# Revit family: 06-44-0035-DN40-600
name_source: partatom
category: Pipe Accessories
units: mm (PartAtom-declared; Revit-internal decimal feet)

## family parameters
Always vertical = No
Cut with Voids When Loaded = No
OmniClass Number = 23.60.00.00
OmniClass Title = General Purpose: Services
Part Type = Valve - Breaks Into
Round Connector Dimension = Use Diameter
Shared = Yes
Work Plane-Based = No

## types (15) — shared parameters
Body_Wallthickness = 15 mm  [stored 0.0492126 ft]
DN040_PN10/16 = 06-040-44-0144299
DN050_PN10/16 = 06-050-44-0144299
DN065_PN10/16 = 06-065-44-0144299
DN080_PN10/16 = 06-080-44-0144299
DN100_PN10/16 = 06-100-44-0144299
DN125_PN10/16 = 06-125-44-0144299
DN150_PN10/16 = 06-150-44-0144299
DN200_PN10 = 06-200-44-0044299
DN200_PN16 = 06-200-44-0144299
DN250_PN10 = 06-250-44-0044299
DN250_PN16 = 06-250-44-0144299
DN300_PN10 = 06-300-44-0044287
DN300_PN16 = 06-300-44-0144287
DN350_PN10 = 06-350-44-00442
DN350_PN16 = 06-350-44-01442
DN400_PN10 = 06-400-44-00442
DN400_PN16 = 06-400-44-01442
DN450_PN10 = 06-450-44-00442
DN450_PN16 = 06-450-44-01442
DN500_PN10 = 06-500-44-00442
DN500_PN16 = 06-500-44-01442
DN600_PN10 = 06-600-44-00442
DN600_PN16 = 06-600-44-01442
Ftc = 4 mm  [stored 0.0131234 ft]
Gearbox_Flangethickness = 10 mm  [stored 0.0328084 ft]
Name_Height_reference = 10 mm  [stored 0.0328084 ft]
Rib_Thickness = 18 mm  [stored 0.0590551 ft]
Search_table = 06-44-0035-DN40-600
Tf = 26 mm
URL product pages = https://www.avkvalves.com
zero-valued in all types: Bottom_Reference

## per-type parameters (varying)
- DN 040: At=57 mm; Body_Height=100 mm; Body_depth=113 mm; Body_width=58 mm; Bonnet_Flange_Depth=127 mm; Bonnet_Flange_Width=90 mm; Bonnet_Flange_cut=8 mm  [stored 0.0262467 ft]; Bonnet_Flange_thickness=15 mm  [stored 0.0492126 ft]; Bonnet_Height=38 mm; Bonnet_Reference_height=90 mm; Bonnet_Thickness=59 mm; Bt=59 mm; Bt_2=52 mm; CL=54 mm; CL _Thickness=10 mm  [stored 0.0328084 ft]; CL_2=24 mm  [stored 0.0787402 ft]; CL_Thickness 2=5 mm  [stored 0.0164042 ft]; Cut_Reference=280 mm; DN 040=Yes; DN 050=No; DN 065=No; DN 080=No; DN 100=No; DN 125=No; DN 150=No; DN 200=No; DN 250=No; DN 300=No; DN 350=No; DN 400=No; DN 450=No; DN 500=No; DN 600=No; Description_=AVK_GATE_VALVE,FLANGED; F=7 mm  [stored 0.0229659 ft]; F1=8 mm  [stored 0.0262467 ft]; F2=30 mm  [stored 0.0984252 ft]; Fillet_Thickness=6 mm  [stored 0.019685 ft]; Flange_OR=75 mm; Flange_Thickness=19 mm  [stored 0.062336 ft]; Flange_Thickness_cut=28 mm  [stored 0.0918635 ft]; Ftc_reference_height=75 mm; Gearbox_Flange_Dia=10 mm  [stored 0.0328084 ft]; H=194 mm; H3=269 mm; Horizontal_Flange_width=150 mm; ID (Radius)=20 mm  [stored 0.0656168 ft]; L=140 mm; L_Dia=40 mm  [stored 0.131234 ft]; Name_Reference=80 mm; Name_Width=29 mm  [stored 0.0951444 ft]; Nominal Diameter (DN)=40 mm  [stored 0.131234 ft]; R1tv=750 mm; R2f=15 mm  [stored 0.0492126 ft]; RF_Dia=42 mm  [stored 0.137795 ft]; Rf=250 mm; Rib_Height_Reference_1=120 mm; Rib_Height_Reference_2=110 mm; Rib_Height_Reference_3=100 mm; Rib_Height_Reference_4=40 mm  [stored 0.131234 ft]; Rib_Width_1=29 mm  [stored 0.0951444 ft]; Rib_Width_2=29 mm  [stored 0.0951444 ft]; Rib_Width_3=29 mm  [stored 0.0951444 ft]; Rib_depth_1=29 mm  [stored 0.0951444 ft]; Rib_depth_2=29 mm  [stored 0.0951444 ft]; Rib_depth_3=29 mm  [stored 0.0951444 ft]; Rt=250 mm
- DN 050: At=61 mm; Body_Height=110 mm; Body_depth=121 mm; Body_width=58 mm; Bonnet_Flange_Depth=133 mm; Bonnet_Flange_Width=92 mm; Bonnet_Flange_cut=8 mm  [stored 0.0262467 ft]; Bonnet_Flange_thickness=15 mm  [stored 0.0492126 ft]; Bonnet_Height=41 mm; Bonnet_Reference_height=100 mm; Bonnet_Thickness=59 mm; Bt=59 mm; Bt_2=52 mm; CL=58 mm; CL _Thickness=10 mm  [stored 0.0328084 ft]; CL_2=28 mm  [stored 0.0918635 ft]; CL_Thickness 2=6 mm  [stored 0.019685 ft]; Cut_Reference=300 mm; DN 040=No; DN 050=Yes; DN 065=No; DN 080=No; DN 100=No; DN 125=No; DN 150=No; DN 200=No; DN 250=No; DN 300=No; DN 350=No; DN 400=No; DN 450=No; DN 500=No; DN 600=No; Description_=AVK_GATE_VALVE,FLANGED; F=7 mm  [stored 0.0229659 ft]; F1=8 mm  [stored 0.0262467 ft]; F2=30 mm  [stored 0.0984252 ft]; Fillet_Thickness=6 mm  [stored 0.019685 ft]; Flange_OR=83 mm; Flange_Thickness=19 mm  [stored 0.062336 ft]; Flange_Thickness_cut=29 mm  [stored 0.0951444 ft]; Ftc_reference_height=83 mm; Gearbox_Flange_Dia=10 mm  [stored 0.0328084 ft]; H=208 mm; H3=290 mm; Horizontal_Flange_width=164 mm; ID (Radius)=25 mm  [stored 0.082021 ft]; L=150 mm; L_Dia=50 mm; Name_Reference=90 mm; Name_Width=29 mm  [stored 0.0951444 ft]; Nominal Diameter (DN)=50 mm; R1tv=825 mm; R2f=15 mm  [stored 0.0492126 ft]; RF_Dia=50 mm; Rf=273 mm; Rib_Height_Reference_1=120 mm; Rib_Height_Reference_2=110 mm; Rib_Height_Reference_3=100 mm; Rib_Height_Reference_4=60 mm; Rib_Width_1=29 mm  [stored 0.0951444 ft]; Rib_Width_2=29 mm  [stored 0.0951444 ft]; Rib_Width_3=29 mm  [stored 0.0951444 ft]; Rib_depth_1=29 mm  [stored 0.0951444 ft]; Rib_depth_2=29 mm  [stored 0.0951444 ft]; Rib_depth_3=29 mm  [stored 0.0951444 ft]; Rt=275 mm
- DN 065: At=69 mm; Body_Height=125 mm; Body_depth=137 mm; Body_width=59 mm; Bonnet_Flange_Depth=152 mm; Bonnet_Flange_Width=91 mm; Bonnet_Flange_cut=8 mm  [stored 0.0262467 ft]; Bonnet_Flange_thickness=15 mm  [stored 0.0492126 ft]; Bonnet_Height=46 mm; Bonnet_Reference_height=115 mm; Bonnet_Thickness=60 mm; Bt=60 mm; Bt_2=53 mm; CL=75 mm; CL _Thickness=10 mm  [stored 0.0328084 ft]; CL_2=45 mm  [stored 0.147638 ft]; CL_Thickness 2=5 mm  [stored 0.0164042 ft]; Cut_Reference=340 mm; DN 040=No; DN 050=No; DN 065=Yes; DN 080=Yes; DN 100=Yes; DN 125=Yes; DN 150=Yes; DN 200=Yes; DN 250=Yes; DN 300=Yes; DN 350=Yes; DN 400=Yes; DN 450=Yes; DN 500=Yes; DN 600=Yes; Description_=AVK_GATE-VALVE,FLANGED; F=9 mm; F1=10 mm  [stored 0.0328084 ft]; F2=34 mm  [stored 0.111549 ft]; Fillet_Thickness=6 mm  [stored 0.019685 ft]; Flange_OR=93 mm; Flange_Thickness=19 mm  [stored 0.062336 ft]; Flange_Thickness_cut=30 mm  [stored 0.0984252 ft]; Ftc_reference_height=93 mm; Gearbox_Flange_Dia=10 mm  [stored 0.0328084 ft]; H=244 mm; H3=337 mm; Horizontal_Flange_width=186 mm; ID (Radius)=33 mm; L=170 mm; L_Dia=65 mm; Name_Reference=100 mm; Name_Width=30 mm  [stored 0.0984252 ft]; Nominal Diameter (DN)=65 mm; R1tv=925 mm; R2f=15 mm  [stored 0.0492126 ft]; RF_Dia=59 mm; Rf=310 mm; Rib_Height_Reference_1=120 mm; Rib_Height_Reference_2=110 mm; Rib_Height_Reference_3=100 mm; Rib_Height_Reference_4=75 mm; Rib_Width_1=30 mm  [stored 0.0984252 ft]; Rib_Width_2=30 mm  [stored 0.0984252 ft]; Rib_Width_3=30 mm  [stored 0.0984252 ft]; Rib_depth_1=30 mm  [stored 0.0984252 ft]; Rib_depth_2=30 mm  [stored 0.0984252 ft]; Rib_depth_3=30 mm  [stored 0.0984252 ft]; Rt=308 mm
- DN 080: At=70 mm; Body_Height=155 mm; Body_depth=140 mm; Body_width=58 mm; Bonnet_Flange_Depth=171 mm; Bonnet_Flange_Width=96 mm; Bonnet_Flange_cut=8 mm  [stored 0.0262467 ft]; Bonnet_Flange_thickness=15 mm  [stored 0.0492126 ft]; Bonnet_Height=50 mm; Bonnet_Reference_height=145 mm; Bonnet_Thickness=59 mm; Bt=59 mm; Bt_2=52 mm; CL=83 mm; CL _Thickness=11 mm  [stored 0.0360892 ft]; CL_2=53 mm; CL_Thickness 2=7 mm  [stored 0.0229659 ft]; Cut_Reference=360 mm; DN 040=Yes; DN 050=Yes; DN 065=Yes; DN 080=Yes; DN 100=Yes; DN 125=Yes; DN 150=Yes; DN 200=Yes; DN 250=Yes; DN 300=Yes; DN 350=Yes; DN 400=Yes; DN 450=Yes; DN 500=Yes; DN 600=Yes; Description_=AVK_GATE_VALVE,FLANGED; F=9 mm; F1=10 mm  [stored 0.0328084 ft]; F2=34 mm  [stored 0.111549 ft]; Fillet_Thickness=6 mm  [stored 0.019685 ft]; Flange_OR=100 mm; Flange_Thickness=19 mm  [stored 0.062336 ft]; Flange_Thickness_cut=30 mm  [stored 0.0984252 ft]; Ftc_reference_height=100 mm; Gearbox_Flange_Dia=11 mm  [stored 0.0360892 ft]; H=282 mm; H3=382 mm; Horizontal_Flange_width=200 mm; ID (Radius)=40 mm  [stored 0.131234 ft]; L=180 mm; L_Dia=80 mm; Name_Reference=130 mm; Name_Width=29 mm  [stored 0.0951444 ft]; Nominal Diameter (DN)=80 mm; R1tv=1000 mm; R2f=15 mm  [stored 0.0492126 ft]; RF_Dia=66 mm; Rf=333 mm; Rib_Height_Reference_1=120 mm; Rib_Height_Reference_2=110 mm; Rib_Height_Reference_3=100 mm; Rib_Height_Reference_4=85 mm; Rib_Width_1=29 mm  [stored 0.0951444 ft]; Rib_Width_2=29 mm  [stored 0.0951444 ft]; Rib_Width_3=29 mm  [stored 0.0951444 ft]; Rib_depth_1=29 mm  [stored 0.0951444 ft]; Rib_depth_2=29 mm  [stored 0.0951444 ft]; Rib_depth_3=29 mm  [stored 0.0951444 ft]; Rt=333 mm
- DN 100: At=84 mm; Body_Height=175 mm; Body_depth=168 mm; Body_width=58 mm; Bonnet_Flange_Depth=192 mm; Bonnet_Flange_Width=105 mm; Bonnet_Flange_cut=8 mm  [stored 0.0262467 ft]; Bonnet_Flange_thickness=15 mm  [stored 0.0492126 ft]; Bonnet_Height=55 mm; Bonnet_Reference_height=165 mm; Bonnet_Thickness=59 mm; Bt=59 mm; Bt_2=52 mm; CL=86 mm; CL _Thickness=12 mm  [stored 0.0393701 ft]; CL_2=56 mm; CL_Thickness 2=10 mm  [stored 0.0328084 ft]; Cut_Reference=380 mm; DN 040=Yes; DN 050=Yes; DN 065=Yes; DN 080=Yes; DN 100=Yes; DN 125=Yes; DN 150=Yes; DN 200=Yes; DN 250=Yes; DN 300=Yes; DN 350=Yes; DN 400=Yes; DN 450=Yes; DN 500=Yes; DN 600=Yes; Description_=AVK_GATE_VALVE,FLANGED; F=10 mm  [stored 0.0328084 ft]; F1=11 mm  [stored 0.0360892 ft]; F2=34 mm  [stored 0.111549 ft]; Fillet_Thickness=6 mm  [stored 0.019685 ft]; Flange_OR=110 mm; Flange_Thickness=19 mm  [stored 0.062336 ft]; Flange_Thickness_cut=30 mm  [stored 0.0984252 ft]; Ftc_reference_height=110 mm; Gearbox_Flange_Dia=12 mm  [stored 0.0393701 ft]; H=305 mm; H3=415 mm; Horizontal_Flange_width=220 mm; ID (Radius)=50 mm; L=190 mm; L_Dia=100 mm; Name_Reference=150 mm; Name_Width=29 mm  [stored 0.0951444 ft]; Nominal Diameter (DN)=100 mm; R1tv=1095 mm; R2f=15 mm  [stored 0.0492126 ft]; RF_Dia=78 mm; Rf=367 mm; Rib_Height_Reference_1=120 mm; Rib_Height_Reference_2=110 mm; Rib_Height_Reference_3=100 mm; Rib_Height_Reference_4=90 mm; Rib_Width_1=29 mm  [stored 0.0951444 ft]; Rib_Width_2=29 mm  [stored 0.0951444 ft]; Rib_Width_3=29 mm  [stored 0.0951444 ft]; Rib_depth_1=29 mm  [stored 0.0951444 ft]; Rib_depth_2=29 mm  [stored 0.0951444 ft]; Rib_depth_3=29 mm  [stored 0.0951444 ft]; Rt=365 mm
- DN 150: At=121 mm; Body_Height=200 mm; Body_depth=242 mm; Body_width=70 mm; Bonnet_Flange_Depth=272 mm; Bonnet_Flange_Width=130 mm; Bonnet_Flange_cut=8 mm  [stored 0.0262467 ft]; Bonnet_Flange_thickness=15 mm  [stored 0.0492126 ft]; Bonnet_Height=71 mm; Bonnet_Reference_height=190 mm; Bonnet_Thickness=71 mm; Bt=71 mm; Bt_2=64 mm; CL=156 mm; CL _Thickness=16 mm  [stored 0.0524934 ft]; CL_2=126 mm; CL_Thickness 2=18 mm  [stored 0.0590551 ft]; Cut_Reference=420 mm; DN 040=Yes; DN 050=Yes; DN 065=Yes; DN 080=Yes; DN 100=Yes; DN 125=Yes; DN 150=Yes; DN 200=Yes; DN 250=Yes; DN 300=Yes; DN 350=Yes; DN 400=Yes; DN 450=Yes; DN 500=Yes; DN 600=Yes; Description_=AVK_GATE_VALVE,FLANGED; F=10 mm  [stored 0.0328084 ft]; F1=11 mm  [stored 0.0360892 ft]; F2=34 mm  [stored 0.111549 ft]; Fillet_Thickness=12 mm  [stored 0.0393701 ft]; Flange_OR=143 mm; Flange_Thickness=19 mm  [stored 0.062336 ft]; Flange_Thickness_cut=34 mm  [stored 0.111549 ft]; Ftc_reference_height=143 mm; Gearbox_Flange_Dia=16 mm  [stored 0.0524934 ft]; H=400 mm; H3=543 mm; Horizontal_Flange_width=286 mm; ID (Radius)=75 mm; L=210 mm; L_Dia=150 mm; Name_Reference=170 mm; Name_Width=35 mm  [stored 0.114829 ft]; Nominal Diameter (DN)=150 mm; R1tv=1425 mm; R2f=30 mm  [stored 0.0984252 ft]; RF_Dia=106 mm; Rf=477 mm; Rib_Height_Reference_1=120 mm; Rib_Height_Reference_2=110 mm; Rib_Height_Reference_3=100 mm; Rib_Height_Reference_4=150 mm; Rib_Width_1=35 mm  [stored 0.114829 ft]; Rib_Width_2=35 mm  [stored 0.114829 ft]; Rib_Width_3=35 mm  [stored 0.114829 ft]; Rib_depth_1=35 mm  [stored 0.114829 ft]; Rib_depth_2=35 mm  [stored 0.114829 ft]; Rib_depth_3=35 mm  [stored 0.114829 ft]; Rt=475 mm
- DN 200: At=157 mm; Body_Height=250 mm; Body_depth=314 mm; Body_width=110 mm; Bonnet_Flange_Depth=332 mm; Bonnet_Flange_Width=170 mm; Bonnet_Flange_cut=13 mm; Bonnet_Flange_thickness=25 mm  [stored 0.082021 ft]; Bonnet_Height=85 mm; Bonnet_Reference_height=240 mm; Bonnet_Thickness=112 mm; Bt=112 mm; Bt_2=104 mm; CL=196 mm; CL _Thickness=23 mm; CL_2=166 mm; CL_Thickness 2=32 mm  [stored 0.104987 ft]; Cut_Reference=460 mm; DN 040=Yes; DN 050=Yes; DN 065=Yes; DN 080=Yes; DN 100=Yes; DN 125=Yes; DN 150=Yes; DN 200=Yes; DN 250=Yes; DN 300=Yes; DN 350=Yes; DN 400=Yes; DN 450=Yes; DN 500=Yes; DN 600=Yes; Description_=AVK_GATE_VALVE,FLANGED; F=12 mm  [stored 0.0393701 ft]; F1=14 mm  [stored 0.0459318 ft]; F2=34 mm  [stored 0.111549 ft]; Fillet_Thickness=24 mm  [stored 0.0787402 ft]; Flange_OR=170 mm; Flange_Thickness=20 mm  [stored 0.0656168 ft]; Flange_Thickness_cut=35 mm  [stored 0.114829 ft]; Ftc_reference_height=170 mm; Gearbox_Flange_Dia=23 mm; H=490 mm; H3=660 mm; Horizontal_Flange_width=340 mm; ID (Radius)=100 mm; L=230 mm; L_Dia=200 mm; Name_Reference=200 mm; Name_Width=55 mm; Nominal Diameter (DN)=200 mm; R1tv=1700 mm; R2f=60 mm; RF_Dia=133 mm; Rf=567 mm; Rib_Height_Reference_1=120 mm; Rib_Height_Reference_2=110 mm; Rib_Height_Reference_3=100 mm; Rib_Height_Reference_4=180 mm; Rib_Width_1=55 mm; Rib_Width_2=55 mm; Rib_Width_3=55 mm; Rib_depth_1=55 mm; Rib_depth_2=55 mm; Rib_depth_3=55 mm; Rt=567 mm
- DN 250: At=196 mm; Body_Height=320 mm; Body_depth=392 mm; Body_width=132 mm; Bonnet_Flange_Depth=422 mm; Bonnet_Flange_Width=175 mm; Bonnet_Flange_cut=13 mm; Bonnet_Flange_thickness=25 mm  [stored 0.082021 ft]; Bonnet_Height=100 mm; Bonnet_Reference_height=310 mm; Bonnet_Thickness=135 mm; Bt=135 mm; Bt_2=126 mm; CL=248 mm; CL _Thickness=24 mm  [stored 0.0787402 ft]; CL_2=218 mm; CL_Thickness 2=33 mm; Cut_Reference=500 mm; DN 040=Yes; DN 050=Yes; DN 065=Yes; DN 080=Yes; DN 100=Yes; DN 125=Yes; DN 150=Yes; DN 200=Yes; DN 250=Yes; DN 300=Yes; DN 350=Yes; DN 400=Yes; DN 450=Yes; DN 500=Yes; DN 600=Yes; Description_=AVK_GATE_VALVE,FLANGED; F=14 mm  [stored 0.0459318 ft]; F1=14 mm  [stored 0.0459318 ft]; F2=47 mm; Fillet_Thickness=24 mm  [stored 0.0787402 ft]; Flange_OR=200 mm; Flange_Thickness=22 mm  [stored 0.0721785 ft]; Flange_Thickness_cut=38 mm; Ftc_reference_height=200 mm; Gearbox_Flange_Dia=24 mm  [stored 0.0787402 ft]; H=625 mm; H3=864 mm; Horizontal_Flange_width=478 mm; ID (Radius)=125 mm; L=250 mm; L_Dia=250 mm; Name_Reference=200 mm; Name_Width=66 mm; Nominal Diameter (DN)=250 mm; R1tv=2000 mm; R2f=60 mm; RF_Dia=160 mm; Rf=797 mm; Rib_Height_Reference_1=90 mm; Rib_Height_Reference_2=110 mm; Rib_Height_Reference_3=100 mm; Rib_Height_Reference_4=250 mm; Rib_Width_1=150 mm; Rib_Width_2=66 mm; Rib_Width_3=66 mm; Rib_depth_1=422 mm; Rib_depth_2=66 mm; Rib_depth_3=66 mm; Rt=667 mm
- DN 300: At=209 mm; Body_Height=415 mm; Body_depth=418 mm; Body_width=160 mm; Bonnet_Flange_Depth=448 mm; Bonnet_Flange_Width=200 mm; Bonnet_Flange_cut=18 mm  [stored 0.0590551 ft]; Bonnet_Flange_thickness=35 mm  [stored 0.114829 ft]; Bonnet_Height=114 mm; Bonnet_Reference_height=405 mm; Bonnet_Thickness=163 mm; Bt=163 mm; Bt_2=154 mm; CL=234 mm; CL _Thickness=28 mm  [stored 0.0918635 ft]; CL_2=204 mm; CL_Thickness 2=42 mm  [stored 0.137795 ft]; Cut_Reference=540 mm; DN 040=Yes; DN 050=Yes; DN 065=Yes; DN 080=Yes; DN 100=Yes; DN 125=Yes; DN 150=Yes; DN 200=Yes; DN 250=Yes; DN 300=Yes; DN 350=Yes; DN 400=Yes; DN 450=Yes; DN 500=Yes; DN 600=Yes; Description_=AVK_GATE_VALVE,FLANGED; F=14 mm  [stored 0.0459318 ft]; F1=14 mm  [stored 0.0459318 ft]; F2=47 mm; Fillet_Thickness=24 mm  [stored 0.0787402 ft]; Flange_OR=228 mm; Flange_Thickness=25 mm  [stored 0.082021 ft]; Flange_Thickness_cut=39 mm  [stored 0.127953 ft]; Ftc_reference_height=228 mm; Gearbox_Flange_Dia=28 mm  [stored 0.0918635 ft]; H=706 mm; H3=928 mm; Horizontal_Flange_width=444 mm; ID (Radius)=150 mm; L=270 mm; L_Dia=300 mm; Name_Reference=300 mm; Name_Width=80 mm; Nominal Diameter (DN)=300 mm; R1tv=2275 mm; R2f=60 mm; RF_Dia=185 mm; Rf=740 mm; Rib_Height_Reference_1=113 mm; Rib_Height_Reference_2=285 mm; Rib_Height_Reference_3=100 mm; Rib_Height_Reference_4=325 mm; Rib_Width_1=210 mm; Rib_Width_2=210 mm; Rib_Width_3=80 mm; Rib_depth_1=455 mm; Rib_depth_2=455 mm; Rib_depth_3=80 mm; Rt=758 mm
- DN 350: At=238 mm; Body_Height=550 mm; Body_depth=476 mm; Body_width=150 mm; Bonnet_Flange_Depth=550 mm; Bonnet_Flange_Width=170 mm; Bonnet_Flange_cut=18 mm  [stored 0.0590551 ft]; Bonnet_Flange_thickness=35 mm  [stored 0.114829 ft]; Bonnet_Height=130 mm; Bonnet_Reference_height=540 mm; Bonnet_Thickness=153 mm; Bt=153 mm; Bt_2=144 mm; CL=315 mm; CL _Thickness=23 mm; CL_2=285 mm; CL_Thickness 2=32 mm  [stored 0.104987 ft]; Cut_Reference=580 mm; DN 040=Yes; DN 050=Yes; DN 065=Yes; DN 080=Yes; DN 100=Yes; DN 125=Yes; DN 150=Yes; DN 200=Yes; DN 250=Yes; DN 300=Yes; DN 350=Yes; DN 400=Yes; DN 450=Yes; DN 500=Yes; DN 600=Yes; Description_=AVK_GATE_VALVE,FLANGED; F=16 mm  [stored 0.0524934 ft]; F1=19 mm  [stored 0.062336 ft]; F2=55 mm; Fillet_Thickness=24 mm  [stored 0.0787402 ft]; Flange_OR=260 mm; Flange_Thickness=27 mm  [stored 0.0885827 ft]; Flange_Thickness_cut=43 mm; Ftc_reference_height=260 mm; Gearbox_Flange_Dia=23 mm; H=930 mm; H3=1190 mm; Horizontal_Flange_width=520 mm; ID (Radius)=175 mm; L=290 mm; L_Dia=350 mm; Name_Reference=520 mm; Name_Width=75 mm; Nominal Diameter (DN)=350 mm; R1tv=2600 mm; R2f=60 mm; RF_Dia=215 mm; Rf=867 mm; Rib_Height_Reference_1=84 mm; Rib_Height_Reference_2=204 mm; Rib_Height_Reference_3=338 mm; Rib_Height_Reference_4=459 mm; Rib_Width_1=180 mm; Rib_Width_2=180 mm; Rib_Width_3=180 mm; Rib_depth_1=564 mm; Rib_depth_2=564 mm; Rib_depth_3=564 mm; Rt=867 mm
- DN 400: At=238 mm; Body_Height=535 mm; Body_depth=476 mm; Body_width=150 mm; Bonnet_Flange_Depth=550 mm; Bonnet_Flange_Width=170 mm; Bonnet_Flange_cut=35 mm  [stored 0.114829 ft]; Bonnet_Flange_thickness=70 mm; Bonnet_Height=145 mm; Bonnet_Reference_height=525 mm; Bonnet_Thickness=153 mm; Bt=153 mm; Bt_2=144 mm; CL=360 mm; CL _Thickness=23 mm; CL_2=330 mm; CL_Thickness 2=32 mm  [stored 0.104987 ft]; Cut_Reference=620 mm; DN 040=Yes; DN 050=Yes; DN 065=Yes; DN 080=Yes; DN 100=Yes; DN 125=Yes; DN 150=Yes; DN 200=Yes; DN 250=Yes; DN 300=Yes; DN 350=Yes; DN 400=Yes; DN 450=Yes; DN 500=Yes; DN 600=Yes; Description_=AVK_GATE_VALVE,FLANGED; F=16 mm  [stored 0.0524934 ft]; F1=19 mm  [stored 0.062336 ft]; F2=55 mm; Fillet_Thickness=32 mm  [stored 0.104987 ft]; Flange_OR=290 mm; Flange_Thickness=28 mm  [stored 0.0918635 ft]; Flange_Thickness_cut=45 mm  [stored 0.147638 ft]; Ftc_reference_height=290 mm; Gearbox_Flange_Dia=23 mm; H=960 mm; H3=1241 mm; Horizontal_Flange_width=562 mm; ID (Radius)=200 mm; L=310 mm; L_Dia=400 mm; Name_Reference=475 mm; Name_Width=75 mm; Nominal Diameter (DN)=400 mm; R1tv=2900 mm; R2f=80 mm; RF_Dia=240 mm; Rf=937 mm; Rib_Height_Reference_1=91 mm; Rib_Height_Reference_2=230 mm; Rib_Height_Reference_3=380 mm; Rib_Height_Reference_4=492 mm; Rib_Width_1=180 mm; Rib_Width_2=180 mm; Rib_Width_3=180 mm; Rib_depth_1=564 mm; Rib_depth_2=564 mm; Rib_depth_3=564 mm; Rt=967 mm
- DN 450: At=381 mm; Body_Height=650 mm; Body_depth=762 mm; Body_width=140 mm; Bonnet_Flange_Depth=814 mm; Bonnet_Flange_Width=165 mm; Bonnet_Flange_cut=35 mm  [stored 0.114829 ft]; Bonnet_Flange_thickness=70 mm; Bonnet_Height=160 mm; Bonnet_Reference_height=640 mm; Bonnet_Thickness=143 mm; Bt=143 mm; Bt_2=134 mm; CL=427 mm; CL _Thickness=22 mm  [stored 0.0721785 ft]; CL_2=397 mm; CL_Thickness 2=30 mm  [stored 0.0984252 ft]; Cut_Reference=700 mm; DN 040=Yes; DN 050=Yes; DN 065=Yes; DN 080=Yes; DN 100=Yes; DN 125=Yes; DN 150=Yes; DN 200=Yes; DN 250=Yes; DN 300=Yes; DN 350=Yes; DN 400=Yes; DN 450=Yes; DN 500=Yes; DN 600=Yes; Description_=AVK_GATE_VALVE,FLANGED; F=15 mm  [stored 0.0492126 ft]; F1=19 mm  [stored 0.062336 ft]; F2=75 mm; Fillet_Thickness=32 mm  [stored 0.104987 ft]; Flange_OR=320 mm; Flange_Thickness=30 mm  [stored 0.0984252 ft]; Flange_Thickness_cut=48 mm; Ftc_reference_height=320 mm; Gearbox_Flange_Dia=88 mm; H=1162 mm; H3=1500 mm; Horizontal_Flange_width=676 mm; ID (Radius)=225 mm; L=350 mm; L_Dia=450 mm; Name_Reference=590 mm; Name_Width=70 mm; Nominal Diameter (DN)=450 mm; R1tv=3200 mm; R2f=80 mm; RF_Dia=274 mm; Rf=1127 mm; Rib_Height_Reference_1=172 mm; Rib_Height_Reference_2=310 mm; Rib_Height_Reference_3=475 mm; Rib_Height_Reference_4=595 mm; Rib_Width_1=165 mm; Rib_Width_2=165 mm; Rib_Width_3=165 mm; Rib_depth_1=814 mm; Rib_depth_2=814 mm; Rib_depth_3=814 mm; Rt=1067 mm
- DN 500: At=360 mm; Body_Height=650 mm; Body_depth=719 mm; Body_width=187 mm; Bonnet_Flange_Depth=792 mm; Bonnet_Flange_Width=219 mm; Bonnet_Flange_cut=35 mm  [stored 0.114829 ft]; Bonnet_Flange_thickness=70 mm; Bonnet_Height=179 mm; Bonnet_Reference_height=640 mm; Bonnet_Thickness=191 mm; Bt=191 mm; Bt_2=181 mm; CL=401 mm; CL _Thickness=31 mm; CL_2=371 mm; CL_Thickness 2=48 mm; Cut_Reference=700 mm; DN 040=Yes; DN 050=Yes; DN 065=Yes; DN 080=Yes; DN 100=Yes; DN 125=Yes; DN 150=Yes; DN 200=Yes; DN 250=Yes; DN 300=Yes; DN 350=Yes; DN 400=Yes; DN 450=Yes; DN 500=Yes; DN 600=Yes; Description_=AVK_GATE_VALVE,FLANGED; F=15 mm  [stored 0.0492126 ft]; F1=19 mm  [stored 0.062336 ft]; F2=75 mm; Fillet_Thickness=32 mm  [stored 0.104987 ft]; Flange_OR=358 mm; Flange_Thickness=32 mm  [stored 0.104987 ft]; Flange_Thickness_cut=54 mm; Ftc_reference_height=358 mm; Gearbox_Flange_Dia=88 mm; H=1136 mm; H3=1500 mm; Horizontal_Flange_width=728 mm; ID (Radius)=250 mm; L=350 mm; L_Dia=500 mm; Name_Reference=590 mm; Name_Width=94 mm; Nominal Diameter (DN)=500 mm; R1tv=3575 mm; R2f=80 mm; RF_Dia=305 mm; Rf=1213 mm; Rib_Height_Reference_1=153 mm; Rib_Height_Reference_2=350 mm; Rib_Height_Reference_3=500 mm; Rib_Height_Reference_4=600 mm; Rib_Width_1=210 mm; Rib_Width_2=210 mm; Rib_Width_3=210 mm; Rib_depth_1=834 mm; Rib_depth_2=834 mm; Rib_depth_3=834 mm; Rt=1192 mm
- DN 600: At=408 mm; Body_Height=740 mm; Body_depth=815 mm; Body_width=210 mm; Bonnet_Flange_Depth=891 mm; Bonnet_Flange_Width=247 mm; Bonnet_Flange_cut=35 mm  [stored 0.114829 ft]; Bonnet_Flange_thickness=70 mm; Bonnet_Height=210 mm; Bonnet_Reference_height=730 mm; Bonnet_Thickness=214 mm; Bt=214 mm; Bt_2=204 mm; CL=455 mm; CL _Thickness=36 mm  [stored 0.11811 ft]; CL_2=425 mm; CL_Thickness 2=57 mm; Cut_Reference=780 mm; DN 040=Yes; DN 050=Yes; DN 065=Yes; DN 080=Yes; DN 100=Yes; DN 125=Yes; DN 150=Yes; DN 200=Yes; DN 250=Yes; DN 300=Yes; DN 350=Yes; DN 400=Yes; DN 450=Yes; DN 500=Yes; DN 600=Yes; Description_=AVK_GATE_VALVE,FLANGED; F=15 mm  [stored 0.0492126 ft]; F1=19 mm  [stored 0.062336 ft]; F2=75 mm; Fillet_Thickness=32 mm  [stored 0.104987 ft]; Flange_OR=420 mm; Flange_Thickness=36 mm  [stored 0.11811 ft]; Flange_Thickness_cut=60 mm; Ftc_reference_height=420 mm; Gearbox_Flange_Dia=88 mm; H=1280 mm; H3=1705 mm; Horizontal_Flange_width=850 mm; ID (Radius)=300 mm; L=390 mm; L_Dia=600 mm; Name_Reference=655 mm; Name_Width=105 mm; Nominal Diameter (DN)=600 mm; R1tv=4200 mm; R2f=80 mm; RF_Dia=360 mm; Rf=1417 mm; Rib_Height_Reference_1=180 mm; Rib_Height_Reference_2=308 mm; Rib_Height_Reference_3=491 mm; Rib_Height_Reference_4=674 mm; Rib_Width_1=220 mm; Rib_Width_2=220 mm; Rib_Width_3=220 mm; Rib_depth_1=964 mm; Rib_depth_2=964 mm; Rib_depth_3=964 mm; Rt=1400 mm
- DN 125: At=96 mm; Body_Height=190 mm; Body_depth=192 mm; Body_width=58 mm; Bonnet_Flange_Depth=220 mm; Bonnet_Flange_Width=111 mm; Bonnet_Flange_cut=8 mm  [stored 0.0262467 ft]; Bonnet_Flange_thickness=15 mm  [stored 0.0492126 ft]; Bonnet_Height=63 mm; Bonnet_Reference_height=180 mm; Bonnet_Thickness=59 mm; Bt=59 mm; Bt_2=52 mm; CL=112 mm; CL _Thickness=13 mm; CL_2=82 mm; CL_Thickness 2=12 mm  [stored 0.0393701 ft]; Cut_Reference=400 mm; DN 040=Yes; DN 050=Yes; DN 065=Yes; DN 080=Yes; DN 100=Yes; DN 125=Yes; DN 150=Yes; DN 200=Yes; DN 250=Yes; DN 300=Yes; DN 350=Yes; DN 400=Yes; DN 450=Yes; DN 500=Yes; DN 600=Yes; Description_=AVK_GATE_VALVE,FLANGED; F=10 mm  [stored 0.0328084 ft]; F1=11 mm  [stored 0.0360892 ft]; F2=34 mm  [stored 0.111549 ft]; Fillet_Thickness=6 mm  [stored 0.019685 ft]; Flange_OR=125 mm; Flange_Thickness=19 mm  [stored 0.062336 ft]; Flange_Thickness_cut=31 mm; Ftc_reference_height=125 mm; Gearbox_Flange_Dia=13 mm; H=346 mm; H3=471 mm; Horizontal_Flange_width=250 mm; ID (Radius)=63 mm; L=200 mm; L_Dia=125 mm; Name_Reference=165 mm; Name_Width=29 mm  [stored 0.0951444 ft]; Nominal Diameter (DN)=125 mm; R1tv=1250 mm; R2f=15 mm  [stored 0.0492126 ft]; RF_Dia=92 mm; Rf=417 mm; Rib_Height_Reference_1=120 mm; Rib_Height_Reference_2=110 mm; Rib_Height_Reference_3=100 mm; Rib_Height_Reference_4=120 mm; Rib_Width_1=29 mm  [stored 0.0951444 ft]; Rib_Width_2=29 mm  [stored 0.0951444 ft]; Rib_Width_3=29 mm  [stored 0.0951444 ft]; Rib_depth_1=29 mm  [stored 0.0951444 ft]; Rib_depth_2=29 mm  [stored 0.0951444 ft]; Rib_depth_3=29 mm  [stored 0.0951444 ft]; Rt=417 mm

note: [stored X ft] marks values corroborated as IEEE doubles in the binary element streams (Revit-internal decimal feet)

## geometry (parser evidence)
native form markers: Sweep x4
no freeform markers — native parametric forms only
